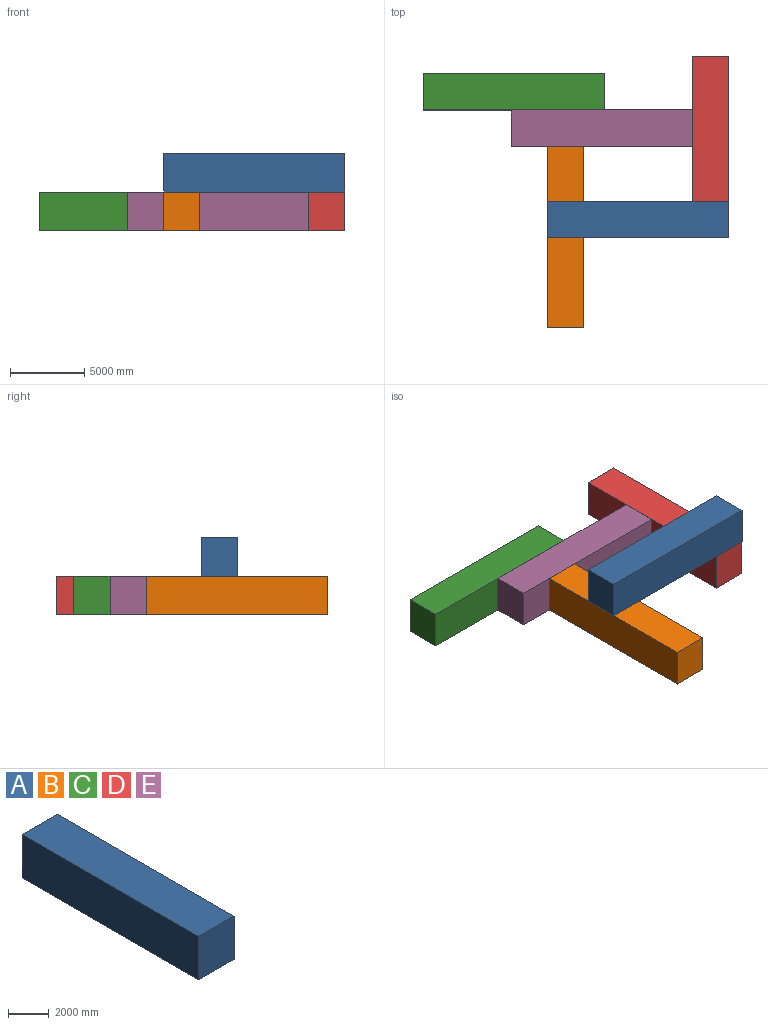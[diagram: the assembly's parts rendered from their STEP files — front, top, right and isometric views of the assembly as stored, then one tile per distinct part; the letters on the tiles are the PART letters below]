
ASSEMBLY  parts=5 mates=10
PART A: 6 faces, bbox 2438.4x12192x2590.8 mm
  f0: plane 12192x2590.8mm, normal (-1,0,0), area 31587033.6mm2, adj f1,f3,f4,f5
  f1: plane 12192x2438.4mm, normal (0,0,-1), area 29728972.8mm2, adj f0,f2,f4,f5
  f2: plane 12192x2590.8mm, normal (1,0,0), area 31587033.6mm2, adj f1,f3,f4,f5
  f3: plane 12192x2438.4mm, normal (0,0,1), area 29728972.8mm2, adj f0,f2,f4,f5
  f4: plane 2590.8x2438.4mm, normal (0,-1,0), area 6317406.7mm2, adj f0,f1,f2,f3
  f5: plane 2590.8x2438.4mm, normal (0,1,0), area 6317406.7mm2, adj f0,f1,f2,f3
PART B: same geometry as A
PART C: same geometry as A
PART D: same geometry as A
PART E: same geometry as A
PLACE A rot(axis=(0,0,-1),90deg) t=(10387.89,3366.57,3280.36)mm
PLACE B t=(-1804.11,7081.61,689.56)mm fixed
PLACE C rot(axis=(0.71,0.71,0),180deg) t=(2026.21,9520.01,3280.36)mm
PLACE D t=(7949.49,13120.17,689.56)mm
PLACE E rot(axis=(0,0,-1),90deg) t=(7949.49,9520.01,689.56)mm
MATE planar D.f3 <-> E.f3  axis (0,0,1) through (9168.69,7024.17,3280.36)mm
MATE planar E.f5 <-> D.f0  axis (1,0,0) through (7949.49,8300.81,1984.96)mm
MATE planar C.f0 <-> E.f0  axis (0,-1,0) through (-4069.79,9520.01,1984.96)mm
MATE planar B.f5 <-> E.f2  axis (0,1,0) through (-584.91,7081.61,1984.96)mm
MATE planar A.f1 <-> D.f3  axis (0,0,-1) through (4291.89,2147.37,3280.36)mm
MATE planar E.f1 <-> B.f1  axis (0,0,-1) through (1853.49,9520.01,689.56)mm
MATE planar C.f1 <-> E.f3  axis (0,0,1) through (-4069.79,11958.41,3280.36)mm
MATE planar A.f5 <-> D.f2  axis (1,0,0) through (10387.89,2147.37,4575.76)mm
MATE planar A.f2 <-> D.f4  axis (0,-1,0) through (4291.89,928.17,4575.76)mm
MATE planar A.f4 <-> B.f0  axis (-1,0,0) through (-1804.11,2147.37,4575.76)mm
